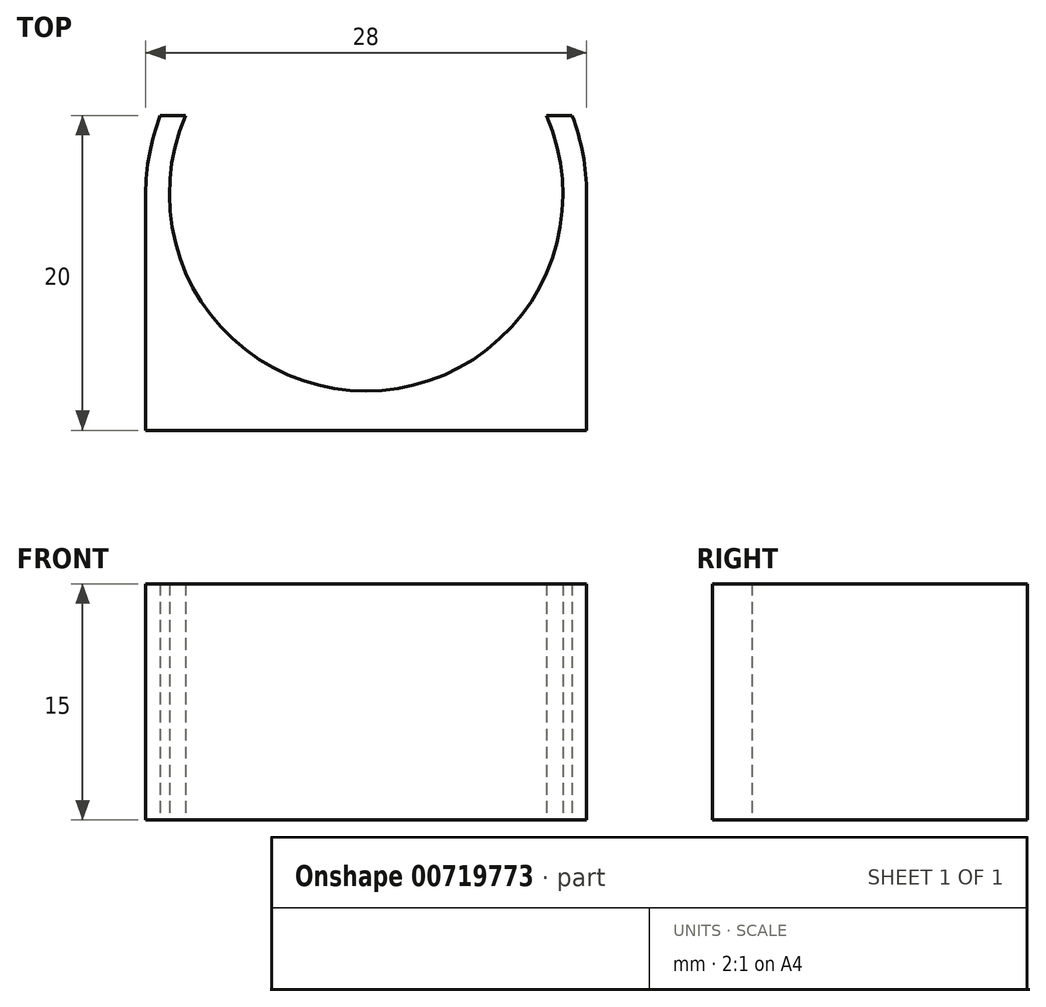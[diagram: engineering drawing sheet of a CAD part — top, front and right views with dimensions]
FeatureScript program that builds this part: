
annotation { "Feature Type Name" : "Feature", "Feature Type Description" : "" }
export const myFeature = defineFeature(function(context is Context, id is Id, definition is map)
    precondition{}
    {
        {
            var Q0;
            Q0=qCreatedBy(makeId("Top.planeOp"),FACE);
            var sketch = newSketch(context, id + "F0", { "sketchPlane" : qUnion([Q0])});
            skArc(sketch, "E0", {"start": v(2.54, 20) * mm, "mid": v(14, 2.5) * mm, "end": v(25.46, 20) * mm});
            skArc(sketch, "E1", {"start": v(0.92, 20) * mm, "mid": v(0.23, 17.54) * mm, "end": v(0, 15) * mm});
            skLineSegment(sketch, "E2", {"start": v(0, 15) * mm, "end": v(0, 0) * mm});
            skLineSegment(sketch, "E3", {"start": v(0.92, 20) * mm, "end": v(27.08, 20) * mm});
            skLineSegment(sketch, "E4", {"start": v(28, 15) * mm, "end": v(28, 0) * mm});
            skLineSegment(sketch, "E5", {"start": v(28, 0) * mm, "end": v(0, 0) * mm});
            skArc(sketch, "E6.trimOffspring", {"start": v(28, 15) * mm, "mid": v(27.77, 17.54) * mm, "end": v(27.08, 20) * mm});
            skSolve(sketch);
        }
        {
            var Q0;
            {var subQ1=sQuery(id+"F0.wireOp",EDGE,"E0");Q0=makeQuery(id+"F0.imprint","IMPRINT",FACE,{"disambiguationData":[TD([[makeQuery(id+"F0.imprint","IMPRINT",EDGE,{"derivedFrom":subQ1}),-1.0]])]});}
            extrude(context, id + "F1", {"entities" : qUnion([Q0]), "depth" : 15 * mm, "offsetDistance" : 25 * mm});
        }
    });
